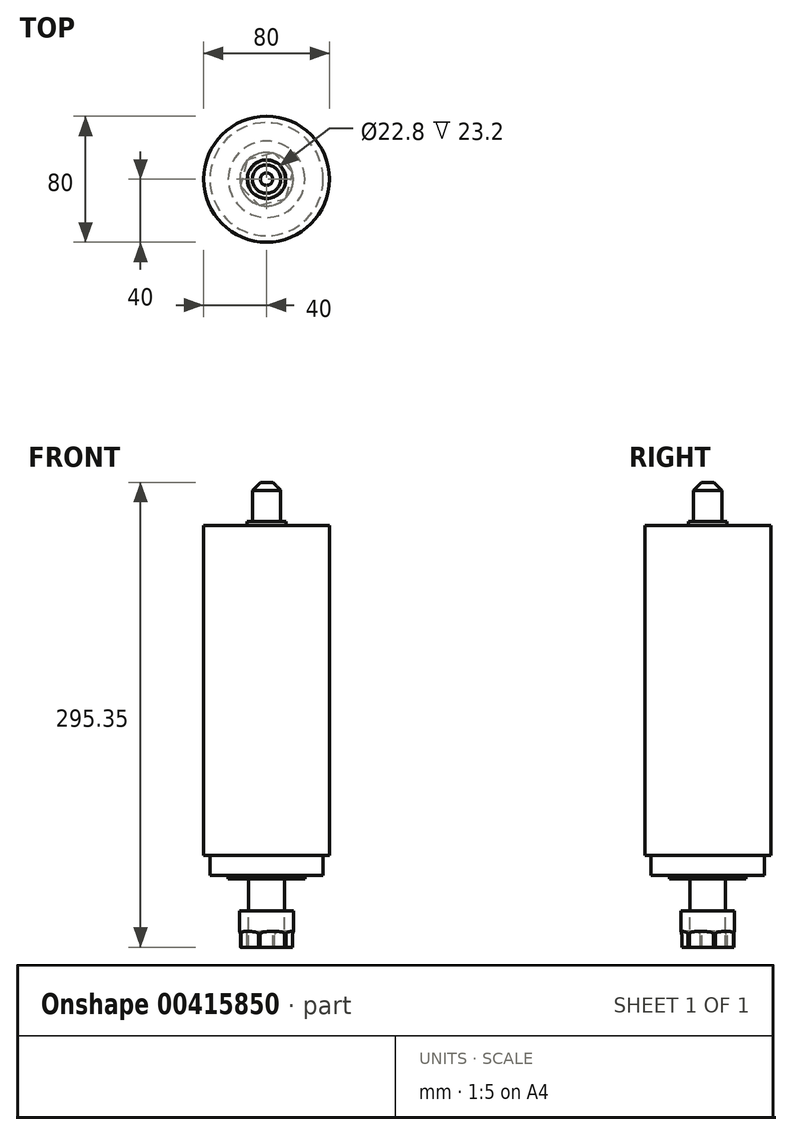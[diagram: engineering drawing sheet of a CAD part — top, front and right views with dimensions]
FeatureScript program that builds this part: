
annotation { "Feature Type Name" : "Feature", "Feature Type Description" : "" }
export const myFeature = defineFeature(function(context is Context, id is Id, definition is map)
    precondition{}
    {
        {
            var Q0;
            Q0=qCreatedBy(makeId("Top.planeOp"),FACE);
            var sketch = newSketch(context, id + "F0", { "sketchPlane" : qUnion([Q0])});
            skCircle(sketch, "E0", {"center": v(0, 0) * mm, "radius": 40 * mm});
            skSolve(sketch);
        }
        {
            var Q0;
            Q0=makeQuery(id+"F0.imprint","IMPRINT",FACE,{"disambiguationData":[TD([[makeQuery(id+"F0.imprint","IMPRINT",EDGE,{"derivedFrom":sQuery(id+"F0.wireOp",EDGE,"E0")}),1.0]])]});
            extrude(context, id + "F1", {"entities" : qUnion([Q0]), "depth" : -171 * mm});
        }
        {
            var Q0;
            Q0=makeQuery(id+"F1.opExtrude","CAP_FACE",FACE,{"disambiguationData":[OSD([sQuery(id+"F0.wireOp",EDGE,"E0")])],"isStart":false});
            var sketch = newSketch(context, id + "F2", { "sketchPlane" : qUnion([Q0])});
            skCircle(sketch, "E1", {"center": v(0, 0) * mm, "radius": 40 * mm});
            skSolve(sketch);
        }
        {
            var Q0;
            Q0=makeQuery(id+"F2.imprint","IMPRINT",FACE,{"disambiguationData":[TD([[makeQuery(id+"F2.imprint","IMPRINT",EDGE,{"derivedFrom":sQuery(id+"F2.wireOp",EDGE,"E1")}),-1.0]])]});
            extrude(context, id + "F3", {"entities" : qUnion([Q0]), "operationType" : NewBodyOperationType.ADD, "depth" : 13.5 * mm});
        }
        {
            var Q0;
            Q0=makeQuery(id+"F3.opExtrude","CAP_FACE",FACE,{"disambiguationData":[OSD([sQuery(id+"F2.wireOp",EDGE,"E1")])],"isStart":false});
            var sketch = newSketch(context, id + "F4", { "sketchPlane" : qUnion([Q0])});
            skCircle(sketch, "E2", {"center": v(0, 0) * mm, "radius": 35.92 * mm});
            skSolve(sketch);
        }
        {
            var Q0;
            Q0=makeQuery(id+"F4.imprint","IMPRINT",FACE,{"disambiguationData":[TD([[makeQuery(id+"F4.imprint","IMPRINT",EDGE,{"derivedFrom":sQuery(id+"F4.wireOp",EDGE,"E2")}),1.0]])]});
            extrude(context, id + "F5", {"entities" : qUnion([Q0]), "operationType" : NewBodyOperationType.ADD, "depth" : 12.5 * mm});
        }
        {
            var Q0;
            Q0=makeQuery(id+"F5.opExtrude","CAP_FACE",FACE,{"disambiguationData":[OSD([sQuery(id+"F4.wireOp",EDGE,"E2")])],"isStart":false});
            var sketch = newSketch(context, id + "F6", { "sketchPlane" : qUnion([Q0])});
            skCircle(sketch, "E3", {"center": v(0, 0) * mm, "radius": 24.3 * mm});
            skSolve(sketch);
        }
        {
            var Q0;
            Q0=makeQuery(id+"F6.imprint","IMPRINT",FACE,{"disambiguationData":[TD([[makeQuery(id+"F6.imprint","IMPRINT",EDGE,{"derivedFrom":sQuery(id+"F6.wireOp",EDGE,"E3")}),1.0]])]});
            extrude(context, id + "F7", {"entities" : qUnion([Q0]), "operationType" : NewBodyOperationType.ADD, "depth" : 2.35 * mm});
        }
        {
            var Q0;
            Q0=makeQuery(id+"F7.opExtrude","CAP_FACE",FACE,{"disambiguationData":[OSD([sQuery(id+"F6.wireOp",EDGE,"E3")])],"isStart":false});
            var sketch = newSketch(context, id + "F8", { "sketchPlane" : qUnion([Q0])});
            skCircle(sketch, "E4", {"center": v(0, 0) * mm, "radius": 11.4 * mm});
            skSolve(sketch);
        }
        {
            var Q0;
            Q0=makeQuery(id+"F8.imprint","IMPRINT",FACE,{"disambiguationData":[TD([[makeQuery(id+"F8.imprint","IMPRINT",EDGE,{"derivedFrom":sQuery(id+"F8.wireOp",EDGE,"E4")}),1.0]])]});
            extrude(context, id + "F9", {"entities" : qUnion([Q0]), "operationType" : NewBodyOperationType.ADD, "depth" : 20.2 * mm});
        }
        {
            var Q0;
            Q0=makeQuery(id+"F9.opExtrude","CAP_FACE",FACE,{"disambiguationData":[OSD([sQuery(id+"F8.wireOp",EDGE,"E4")])],"isStart":false});
            var sketch = newSketch(context, id + "F10", { "sketchPlane" : qUnion([Q0])});
            skCircle(sketch, "E5", {"center": v(0, 0) * mm, "radius": 17 * mm});
            skSolve(sketch);
        }
        {
            var Q0;
            Q0=makeQuery(id+"F10.imprint","IMPRINT",FACE,{"disambiguationData":[TD([[makeQuery(id+"F10.imprint","IMPRINT",EDGE,{"derivedFrom":sQuery(id+"F10.wireOp",EDGE,"E5")}),1.0]])]});
            extrude(context, id + "F11", {"entities" : qUnion([Q0]), "depth" : 13.2 * mm});
        }
        {
            var Q0;
            Q0=makeQuery(id+"F11.opExtrude","CAP_FACE",FACE,{"disambiguationData":[OSD([sQuery(id+"F8.wireOp",EDGE,"E4"),sQuery(id+"F10.wireOp",EDGE,"E5")])],"isStart":false});
            var sketch = newSketch(context, id + "F12", { "sketchPlane" : qUnion([Q0])});
            skCircle(sketch, "E6.cCircle", {"center": v(0, 0) * mm, "radius": 15 * mm, "construction": true});
            skLineSegment(sketch, "E6.0", {"start": v(-12.1, -12.4) * mm, "end": v(-16.79, 4.27) * mm});
            skLineSegment(sketch, "E6.1", {"start": v(-16.79, 4.27) * mm, "end": v(-4.7, 16.67) * mm});
            skLineSegment(sketch, "E6.2", {"start": v(-4.7, 16.67) * mm, "end": v(12.1, 12.4) * mm});
            skLineSegment(sketch, "E6.3", {"start": v(12.1, 12.4) * mm, "end": v(16.79, -4.27) * mm});
            skLineSegment(sketch, "E6.4", {"start": v(16.79, -4.27) * mm, "end": v(4.7, -16.67) * mm});
            skLineSegment(sketch, "E6.5", {"start": v(4.7, -16.67) * mm, "end": v(-12.1, -12.4) * mm});
            skPoint(sketch, "E6.0.midPoint", {"position": v(-14.44, -4.06) * mm});
            skSolve(sketch);
        }
        {
            var Q0;
            Q0=makeQuery(id+"F12.imprint","IMPRINT",FACE,{"disambiguationData":[TD([[makeQuery(id+"F12.imprint","IMPRINT",EDGE,{"derivedFrom":makeQuery(id+"F11.opExtrude","CAP_EDGE",EDGE,{"disambiguationData":[OSD([sQuery(id+"F8.wireOp",EDGE,"E4")])],"isStart":false})}),-1.0]])]});
            extrude(context, id + "F13", {"entities" : qUnion([Q0]), "operationType" : NewBodyOperationType.ADD, "depth" : 10 * mm});
        }
        {
            var Q0;
            Q0=makeQuery(id+"F13.opExtrude","CAP_EDGE",EDGE,{"disambiguationData":[OSD([sQuery(id+"F12.wireOp",EDGE,"E6.2")])],"isStart":true});
            var Q1;
            Q1=makeQuery(id+"F13.opExtrude","CAP_EDGE",EDGE,{"disambiguationData":[OSD([sQuery(id+"F12.wireOp",EDGE,"E6.3")])],"isStart":true});
            var Q2;
            Q2=makeQuery(id+"F13.opExtrude","CAP_EDGE",EDGE,{"disambiguationData":[OSD([sQuery(id+"F12.wireOp",EDGE,"E6.4")])],"isStart":true});
            var Q3;
            Q3=makeQuery(id+"F13.opExtrude","CAP_EDGE",EDGE,{"disambiguationData":[OSD([sQuery(id+"F12.wireOp",EDGE,"E6.5")])],"isStart":true});
            var Q4;
            Q4=makeQuery(id+"F13.opExtrude","CAP_EDGE",EDGE,{"disambiguationData":[OSD([sQuery(id+"F12.wireOp",EDGE,"E6.0")])],"isStart":true});
            var Q5;
            Q5=makeQuery(id+"F13.opExtrude","CAP_EDGE",EDGE,{"disambiguationData":[OSD([sQuery(id+"F12.wireOp",EDGE,"E6.1")])],"isStart":true});
            fillet(context, id + "F14", {"entities" : qUnion([Q0, Q1, Q2, Q3, Q4, Q5]), "radius" : 2 * mm, "tangentPropagation" : true, "allowEdgeOverflow" : false});
        }
        {
            var Q0;
            Q0=makeQuery(id+"F1.opExtrude","CAP_FACE",FACE,{"disambiguationData":[OSD([sQuery(id+"F0.wireOp",EDGE,"E0")])],"isStart":true});
            var sketch = newSketch(context, id + "F15", { "sketchPlane" : qUnion([Q0])});
            skSolve(sketch);
        }
        {
            var Q0;
            Q0=makeQuery(id+"F15.imprint","IMPRINT",FACE,{"disambiguationData":[TD([[makeQuery(id+"F15.imprint","IMPRINT",EDGE,{"derivedFrom":makeQuery(id+"F1.opExtrude","CAP_EDGE",EDGE,{"disambiguationData":[OSD([sQuery(id+"F0.wireOp",EDGE,"E0")])],"isStart":true})}),1.0]])]});
            extrude(context, id + "F16", {"entities" : qUnion([Q0]), "operationType" : NewBodyOperationType.ADD, "depth" : 25 * mm});
        }
        {
            var Q0;
            Q0=makeQuery(id+"F16.opExtrude","CAP_FACE",FACE,{"disambiguationData":[OSD([sQuery(id+"F0.wireOp",EDGE,"E0")])],"isStart":false});
            var sketch = newSketch(context, id + "F17", { "sketchPlane" : qUnion([Q0])});
            skCircle(sketch, "E7", {"center": v(0, 0) * mm, "radius": 12.25 * mm});
            skSolve(sketch);
        }
        {
            var Q0;
            Q0=makeQuery(id+"F17.imprint","IMPRINT",FACE,{"disambiguationData":[TD([[makeQuery(id+"F17.imprint","IMPRINT",EDGE,{"derivedFrom":sQuery(id+"F17.wireOp",EDGE,"E7")}),1.0]])]});
            extrude(context, id + "F18", {"entities" : qUnion([Q0]), "operationType" : NewBodyOperationType.ADD, "depth" : 2.6 * mm});
        }
        {
            var Q0;
            Q0=makeQuery(id+"F18.opExtrude","CAP_FACE",FACE,{"disambiguationData":[OSD([sQuery(id+"F17.wireOp",EDGE,"E7")])],"isStart":false});
            var sketch = newSketch(context, id + "F19", { "sketchPlane" : qUnion([Q0])});
            skCircle(sketch, "E8", {"center": v(0, 0) * mm, "radius": 9 * mm});
            skSolve(sketch);
        }
        {
            var Q0;
            Q0=makeQuery(id+"F19.imprint","IMPRINT",FACE,{"disambiguationData":[TD([[makeQuery(id+"F19.imprint","IMPRINT",EDGE,{"derivedFrom":sQuery(id+"F19.wireOp",EDGE,"E8")}),1.0]])]});
            extrude(context, id + "F20", {"entities" : qUnion([Q0]), "operationType" : NewBodyOperationType.ADD, "depth" : 25 * mm});
        }
        {
            var Q0;
            Q0=makeQuery(id+"F20.opExtrude","CAP_EDGE",EDGE,{"disambiguationData":[OSD([sQuery(id+"F19.wireOp",EDGE,"E8")])],"isStart":false});
            chamfer(context, id + "F21", {"entities" : qUnion([Q0]), "width" : 5.08 * mm, "tangentPropagation" : true});
        }
    });
